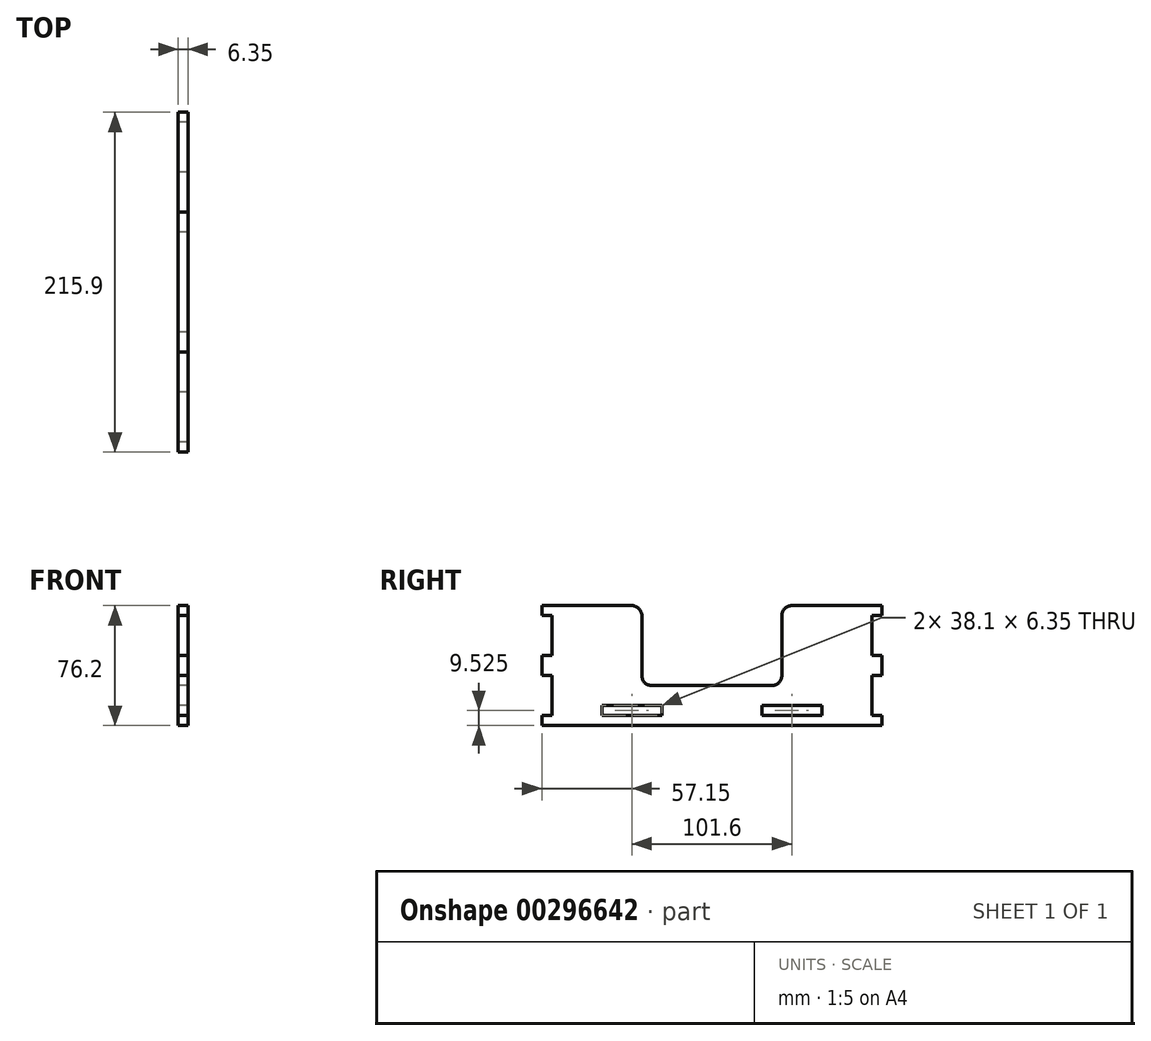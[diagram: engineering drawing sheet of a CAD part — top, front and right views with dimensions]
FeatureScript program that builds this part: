
annotation { "Feature Type Name" : "Feature", "Feature Type Description" : "" }
export const myFeature = defineFeature(function(context is Context, id is Id, definition is map)
    precondition{}
    {
        {
            var Q0;
            Q0=qCreatedBy(makeId("Right.planeOp"),FACE);
            var sketch = newSketch(context, id + "F0", { "sketchPlane" : qUnion([Q0])});
            skLineSegment(sketch, "E0.bottom", {"start": v(-107.95, 38.1) * mm, "end": v(-44.45, 38.1) * mm});
            skLineSegment(sketch, "E0.top", {"start": v(-107.95, -38.1) * mm, "end": v(107.95, -38.1) * mm});
            skLineSegment(sketch, "E0.left", {"start": v(-107.95, 38.1) * mm, "end": v(-107.95, 31.75) * mm});
            skLineSegment(sketch, "E0.right", {"start": v(107.95, 38.1) * mm, "end": v(107.95, 31.75) * mm});
            skPoint(sketch, "E0.middle", {"position": v(0, 0) * mm});
            skLineSegment(sketch, "E1", {"start": v(-107.95, -28.58) * mm, "end": v(107.95, -28.58) * mm, "construction": true});
            skLineSegment(sketch, "E2.bottom", {"start": v(-31.75, -25.4) * mm, "end": v(-69.85, -25.4) * mm});
            skLineSegment(sketch, "E2.top", {"start": v(-31.75, -31.75) * mm, "end": v(-69.85, -31.75) * mm});
            skLineSegment(sketch, "E2.left", {"start": v(-31.75, -25.4) * mm, "end": v(-31.75, -31.75) * mm});
            skLineSegment(sketch, "E2.right", {"start": v(-69.85, -25.4) * mm, "end": v(-69.85, -31.75) * mm});
            skPoint(sketch, "E2.middle", {"position": v(-50.8, -28.58) * mm});
            skLineSegment(sketch, "E3.MirrorCS", {"start": v(31.75, -31.75) * mm, "end": v(69.85, -31.75) * mm});
            skLineSegment(sketch, "E4.MirrorCS", {"start": v(31.75, -25.4) * mm, "end": v(31.75, -31.75) * mm});
            skLineSegment(sketch, "E5.MirrorCS", {"start": v(69.85, -25.4) * mm, "end": v(69.85, -31.75) * mm});
            skLineSegment(sketch, "E6.MirrorCS", {"start": v(31.75, -25.4) * mm, "end": v(69.85, -25.4) * mm});
            skPoint(sketch, "E7.MirrorP", {"position": v(50.8, -28.58) * mm});
            skLineSegment(sketch, "E8.top", {"start": v(-44.45, -12.7) * mm, "end": v(44.45, -12.7) * mm});
            skLineSegment(sketch, "E8.left", {"start": v(-44.45, 38.1) * mm, "end": v(-44.45, -12.7) * mm});
            skLineSegment(sketch, "E8.right", {"start": v(44.45, 38.1) * mm, "end": v(44.45, -12.7) * mm});
            skLineSegment(sketch, "E9.trimOffspring", {"start": v(44.45, 38.1) * mm, "end": v(107.95, 38.1) * mm});
            skPoint(sketch, "E10", {"position": v(0, -12.7) * mm});
            skLineSegment(sketch, "E11.bottom", {"start": v(-107.95, 31.75) * mm, "end": v(-101.6, 31.75) * mm});
            skLineSegment(sketch, "E11.top", {"start": v(-107.95, 6.35) * mm, "end": v(-101.6, 6.35) * mm});
            skLineSegment(sketch, "E11.right", {"start": v(-101.6, 31.75) * mm, "end": v(-101.6, 6.35) * mm});
            skLineSegment(sketch, "E12.bottom", {"start": v(-107.95, -6.35) * mm, "end": v(-101.6, -6.35) * mm});
            skLineSegment(sketch, "E12.top", {"start": v(-107.95, -31.75) * mm, "end": v(-101.6, -31.75) * mm});
            skLineSegment(sketch, "E12.right", {"start": v(-101.6, -6.35) * mm, "end": v(-101.6, -31.75) * mm});
            skPoint(sketch, "E13", {"position": v(-107.95, 0) * mm});
            skPoint(sketch, "E14", {"position": v(-101.6, 19.05) * mm});
            skPoint(sketch, "E15", {"position": v(-101.6, -19.05) * mm});
            skLineSegment(sketch, "E16.MirrorCS", {"start": v(107.95, 31.75) * mm, "end": v(101.6, 31.75) * mm});
            skLineSegment(sketch, "E17.MirrorCS", {"start": v(107.95, -6.35) * mm, "end": v(101.6, -6.35) * mm});
            skLineSegment(sketch, "E18.MirrorCS", {"start": v(107.95, -31.75) * mm, "end": v(101.6, -31.75) * mm});
            skLineSegment(sketch, "E19.MirrorCS", {"start": v(107.95, 6.35) * mm, "end": v(101.6, 6.35) * mm});
            skPoint(sketch, "E20.MirrorP", {"position": v(107.95, 0) * mm});
            skPoint(sketch, "E21.MirrorP", {"position": v(101.6, -19.05) * mm});
            skLineSegment(sketch, "E22.MirrorCS", {"start": v(101.6, 31.75) * mm, "end": v(101.6, 6.35) * mm});
            skPoint(sketch, "E23.MirrorP", {"position": v(101.6, 19.05) * mm});
            skLineSegment(sketch, "E24.MirrorCS", {"start": v(101.6, -6.35) * mm, "end": v(101.6, -31.75) * mm});
            skLineSegment(sketch, "E25.trimOffspring", {"start": v(-107.95, 6.35) * mm, "end": v(-107.95, -6.35) * mm});
            skLineSegment(sketch, "E26.trimOffspring", {"start": v(-107.95, -31.75) * mm, "end": v(-107.95, -38.1) * mm});
            skLineSegment(sketch, "E27.trimOffspring", {"start": v(107.95, -31.75) * mm, "end": v(107.95, -38.1) * mm});
            skLineSegment(sketch, "E28.trimOffspring", {"start": v(107.95, 6.35) * mm, "end": v(107.95, -6.35) * mm});
            skSolve(sketch);
        }
        {
            var Q0;
            Q0 = qSketchRegion(id + "F0", true);
            extrude(context, id + "F1", {"entities" : qUnion([Q0]), "depth" : 6.35 * mm});
        }
        {
            var Q0;
            Q0=makeQuery(id+"F1.opExtrude","SWEPT_EDGE",EDGE,{"disambiguationData":[OSD([sQuery(id+"F0.wireOp",EDGE,"E0.bottom"),sQuery(id+"F0.wireOp",EDGE,"E8.left")])]});
            var Q1;
            Q1=makeQuery(id+"F1.opExtrude","SWEPT_EDGE",EDGE,{"disambiguationData":[OSD([sQuery(id+"F0.wireOp",EDGE,"E8.top"),sQuery(id+"F0.wireOp",EDGE,"E8.left")])]});
            var Q2;
            Q2=makeQuery(id+"F1.opExtrude","SWEPT_EDGE",EDGE,{"disambiguationData":[OSD([sQuery(id+"F0.wireOp",EDGE,"E8.right"),sQuery(id+"F0.wireOp",EDGE,"E9.trimOffspring")])]});
            var Q3;
            Q3=makeQuery(id+"F1.opExtrude","SWEPT_EDGE",EDGE,{"disambiguationData":[OSD([sQuery(id+"F0.wireOp",EDGE,"E8.top"),sQuery(id+"F0.wireOp",EDGE,"E8.right")])]});
            fillet(context, id + "F2", {"entities" : qUnion([Q0, Q1, Q2, Q3]), "radius" : 6.35 * mm, "tangentPropagation" : true, "allowEdgeOverflow" : false});
        }
    });
